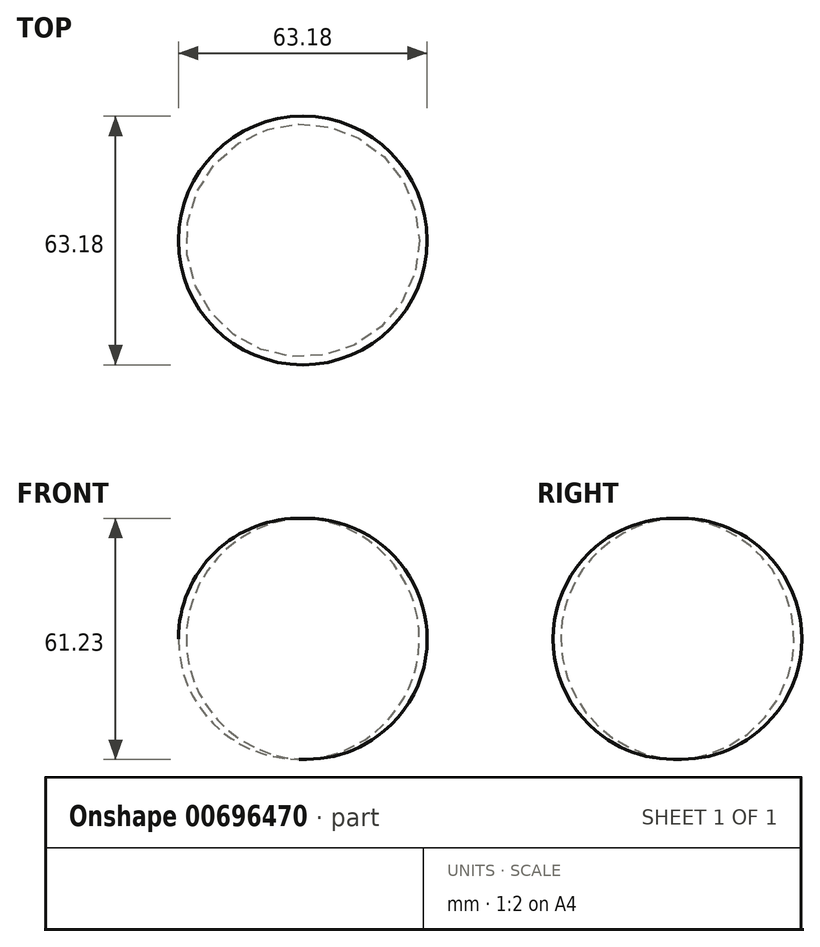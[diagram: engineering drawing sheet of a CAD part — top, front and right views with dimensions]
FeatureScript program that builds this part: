
annotation { "Feature Type Name" : "Feature", "Feature Type Description" : "" }
export const myFeature = defineFeature(function(context is Context, id is Id, definition is map)
    precondition{}
    {
        {
            var Q0;
            Q0=qCreatedBy(makeId("Front.planeOp"),FACE);
            var sketch = newSketch(context, id + "F0", { "sketchPlane" : qUnion([Q0])});
            skLineSegment(sketch, "E0", {"start": v(0, 0) * mm, "end": v(0, 61.19) * mm});
            skArc(sketch, "E1", {"start": v(0, 61.19) * mm, "mid": v(-31.6, 30.6) * mm, "end": v(0, 0) * mm});
            skSolve(sketch);
        }
        {
            var Q0;
            Q0=makeQuery(id+"F0.imprint","IMPRINT",FACE,{"disambiguationData":[TD([[makeQuery(id+"F0.imprint","IMPRINT",EDGE,{"derivedFrom":sQuery(id+"F0.wireOp",EDGE,"E0")}),1.0]])]});
            var Q1;
            Q1=sQuery(id+"F0.wireOp",EDGE,"E0");
            revolve(context, id + "F1", {"entities" : qUnion([Q0]), "axis" : qUnion([Q1]), "revolveType" : RevolveType.FULL});
        }
    });
